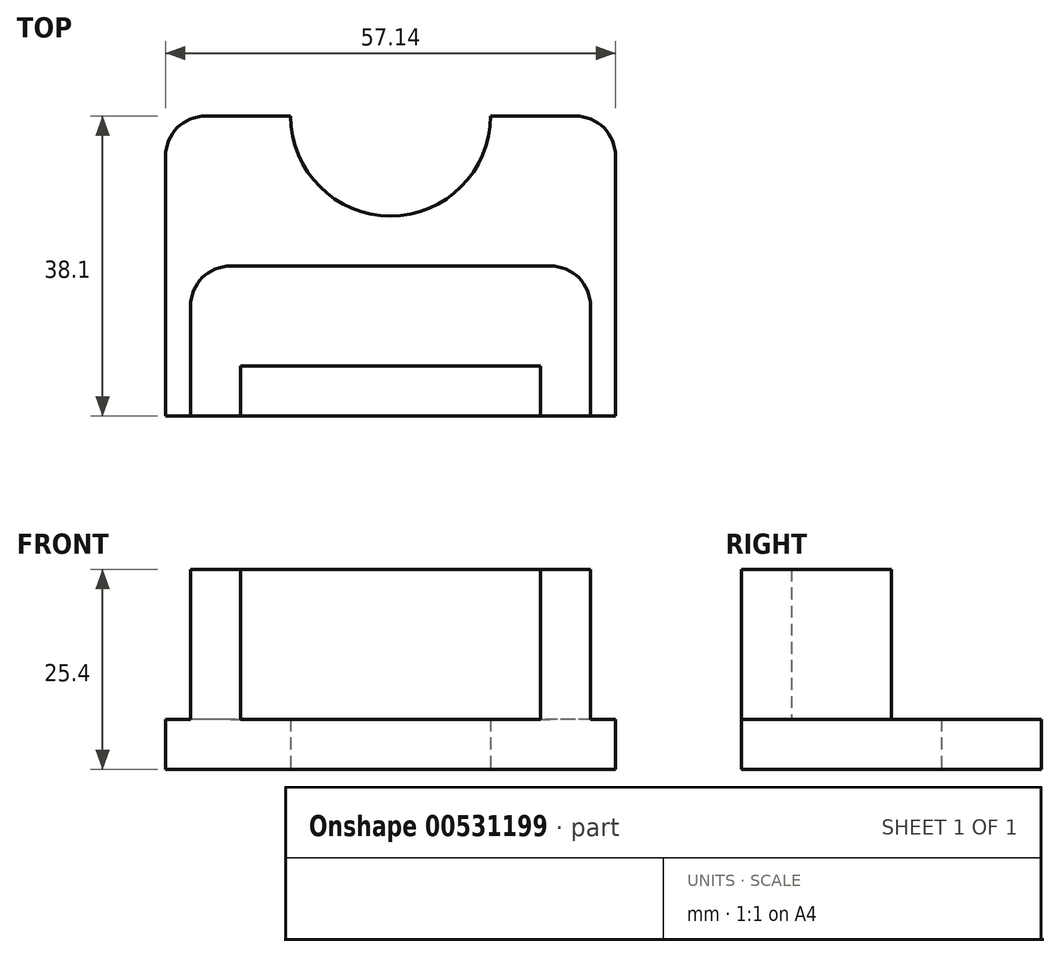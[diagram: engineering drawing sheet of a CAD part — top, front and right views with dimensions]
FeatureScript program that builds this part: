
annotation { "Feature Type Name" : "Feature", "Feature Type Description" : "" }
export const myFeature = defineFeature(function(context is Context, id is Id, definition is map)
    precondition{}
    {
        {
            var Q0;
            Q0=qCreatedBy(makeId("Top.planeOp"),FACE);
            var sketch = newSketch(context, id + "F0", { "sketchPlane" : qUnion([Q0])});
            skLineSegment(sketch, "E0.bottom", {"start": v(28.58, 19.05) * mm, "end": v(-28.58, 19.05) * mm});
            skLineSegment(sketch, "E0.top", {"start": v(28.58, -19.05) * mm, "end": v(-28.58, -19.05) * mm});
            skLineSegment(sketch, "E0.left", {"start": v(28.58, 19.05) * mm, "end": v(28.58, -19.05) * mm});
            skLineSegment(sketch, "E0.right", {"start": v(-28.58, 19.05) * mm, "end": v(-28.58, -19.05) * mm});
            skPoint(sketch, "E0.middle", {"position": v(0, 0) * mm});
            skCircle(sketch, "E1", {"center": v(0, 19.05) * mm, "radius": 12.7 * mm});
            skSolve(sketch);
        }
        {
            var Q0;
            Q0=makeQuery(id+"F0.imprint","IMPRINT",FACE,{"disambiguationData":[TD([[makeQuery(id+"F0.imprint","IMPRINT",EDGE,{"derivedFrom":sQuery(id+"F0.wireOp",EDGE,"E0.top")}),-1.0]])]});
            extrude(context, id + "F1", {"entities" : qUnion([Q0]), "depth" : 6.35 * mm, "offsetDistance" : 25.4 * mm});
        }
        {
            var Q0;
            Q0=makeQuery(id+"F1.opExtrude","CAP_FACE",FACE,{"disambiguationData":[OSD([sQuery(id+"F0.wireOp",EDGE,"E0.bottom"),sQuery(id+"F0.wireOp",EDGE,"E0.top"),sQuery(id+"F0.wireOp",EDGE,"E0.left"),sQuery(id+"F0.wireOp",EDGE,"E0.right"),sQuery(id+"F0.wireOp",EDGE,"E1")])],"isStart":false});
            var sketch = newSketch(context, id + "F2", { "sketchPlane" : qUnion([Q0])});
            skLineSegment(sketch, "E2.bottom", {"start": v(-25.4, -19.05) * mm, "end": v(25.4, -19.05) * mm});
            skLineSegment(sketch, "E2.top", {"start": v(-25.4, 0) * mm, "end": v(25.4, 0) * mm});
            skLineSegment(sketch, "E2.left", {"start": v(-25.4, -19.05) * mm, "end": v(-25.4, 0) * mm});
            skLineSegment(sketch, "E2.right", {"start": v(25.4, -19.05) * mm, "end": v(25.4, 0) * mm});
            skLineSegment(sketch, "E3.bottom", {"start": v(-15.88, 19.05) * mm, "end": v(15.88, 19.05) * mm});
            skLineSegment(sketch, "E3.top", {"start": v(-15.88, 0) * mm, "end": v(15.88, 0) * mm});
            skLineSegment(sketch, "E3.left", {"start": v(-15.88, 19.05) * mm, "end": v(-15.88, 0) * mm});
            skLineSegment(sketch, "E3.right", {"start": v(15.88, 19.05) * mm, "end": v(15.88, 0) * mm});
            skLineSegment(sketch, "E4.bottom", {"start": v(-19.05, -19.05) * mm, "end": v(19.05, -19.05) * mm});
            skLineSegment(sketch, "E4.top", {"start": v(-19.05, -12.7) * mm, "end": v(19.05, -12.7) * mm});
            skLineSegment(sketch, "E4.left", {"start": v(-19.05, -19.05) * mm, "end": v(-19.05, -12.7) * mm});
            skLineSegment(sketch, "E4.right", {"start": v(19.05, -19.05) * mm, "end": v(19.05, -12.7) * mm});
            skSolve(sketch);
        }
        {
            var Q0;
            Q0=makeQuery(id+"F2.imprint","IMPRINT",FACE,{"disambiguationData":[TD([[makeQuery(id+"F2.imprint","IMPRINT",EDGE,{"derivedFrom":sQuery(id+"F2.wireOp",EDGE,"E3.top")}),1.0]])]});
            var Q1;
            Q1=makeQuery(id+"F2.imprint","IMPRINT",FACE,{"disambiguationData":[TD([[makeQuery(id+"F2.imprint","IMPRINT",EDGE,{"derivedFrom":sQuery(id+"F2.wireOp",EDGE,"E2.bottom")}),-1.0]])]});
            extrude(context, id + "F3", {"entities" : qUnion([Q0, Q1]), "operationType" : NewBodyOperationType.ADD, "depth" : 19.05 * mm, "offsetDistance" : 25.4 * mm});
        }
        {
            var Q0;
            Q0=makeQuery(id+"F1.opExtrude","SWEPT_EDGE",EDGE,{"disambiguationData":[OSD([sQuery(id+"F0.wireOp",EDGE,"E0.bottom"),sQuery(id+"F0.wireOp",EDGE,"E0.right")])]});
            var Q1;
            Q1=makeQuery(id+"F1.opExtrude","SWEPT_EDGE",EDGE,{"disambiguationData":[OSD([sQuery(id+"F0.wireOp",EDGE,"E0.bottom"),sQuery(id+"F0.wireOp",EDGE,"E0.left")])]});
            var Q2;
            Q2=makeQuery(id+"F3.opExtrude","SWEPT_EDGE",EDGE,{"disambiguationData":[OSD([sQuery(id+"F2.wireOp",EDGE,"E2.top"),sQuery(id+"F2.wireOp",EDGE,"E3.top"),sQuery(id+"F2.wireOp",EDGE,"E3.left")])]});
            var Q3;
            Q3=makeQuery(id+"F3.opExtrude","SWEPT_EDGE",EDGE,{"disambiguationData":[OSD([sQuery(id+"F2.wireOp",EDGE,"E2.top"),sQuery(id+"F2.wireOp",EDGE,"E3.top"),sQuery(id+"F2.wireOp",EDGE,"E3.right")])]});
            fillet(context, id + "F4", {"entities" : qUnion([Q0, Q1, Q2, Q3]), "radius" : 5.08 * mm, "tangentPropagation" : true, "allowEdgeOverflow" : false});
        }
    });
